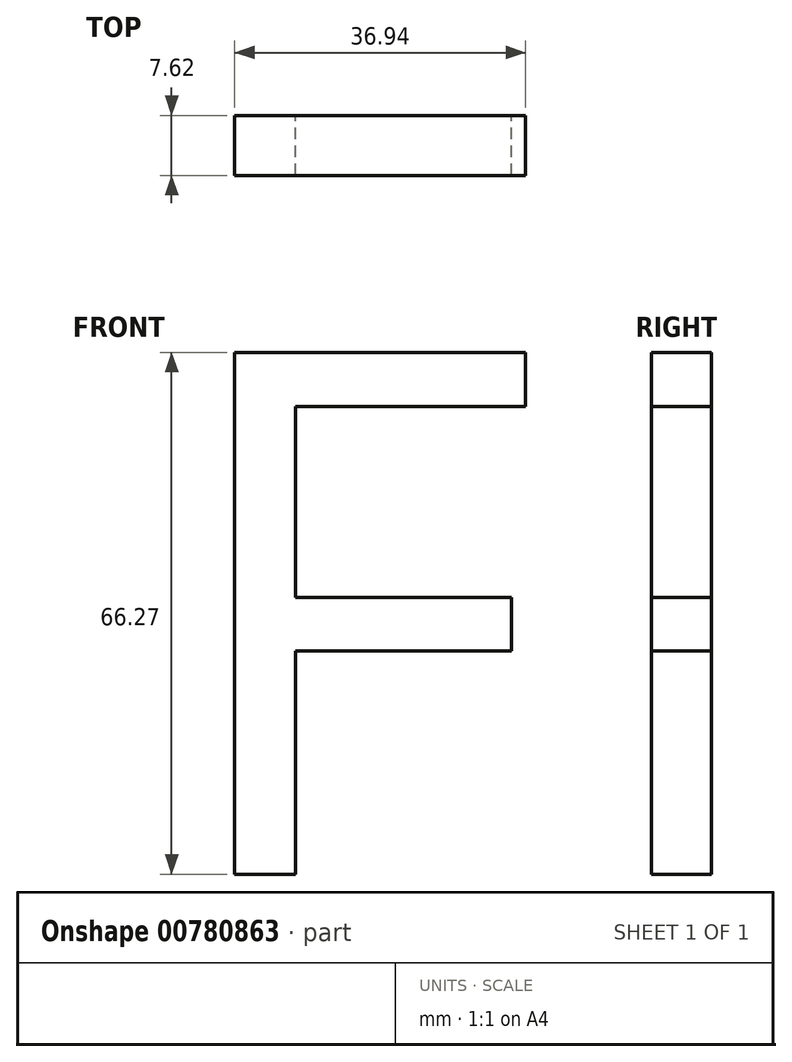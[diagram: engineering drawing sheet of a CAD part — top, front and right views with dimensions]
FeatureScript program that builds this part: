
annotation { "Feature Type Name" : "Feature", "Feature Type Description" : "" }
export const myFeature = defineFeature(function(context is Context, id is Id, definition is map)
    precondition{}
    {
        {
            var Q0;
            Q0=qCreatedBy(makeId("Front.planeOp"),FACE);
            var sketch = newSketch(context, id + "F0", { "sketchPlane" : qUnion([Q0])});
            skText(sketch, "E0", { "text": "F", "fontName": "OpenSans-Regular.ttf"});
            const initialGuessF0  = {"E0": [-0.03077, -0.02748, 1, 0, 0.06684]};
            skSetInitialGuess(sketch, initialGuessF0);
            skSolve(sketch);
        }
        {
            var Q0;
            Q0 = qSketchRegion(id + "F0", true);
            extrude(context, id + "F1", {"entities" : qUnion([Q0]), "depth" : 7.62 * mm, "offsetDistance" : 25.4 * mm});
        }
    });
